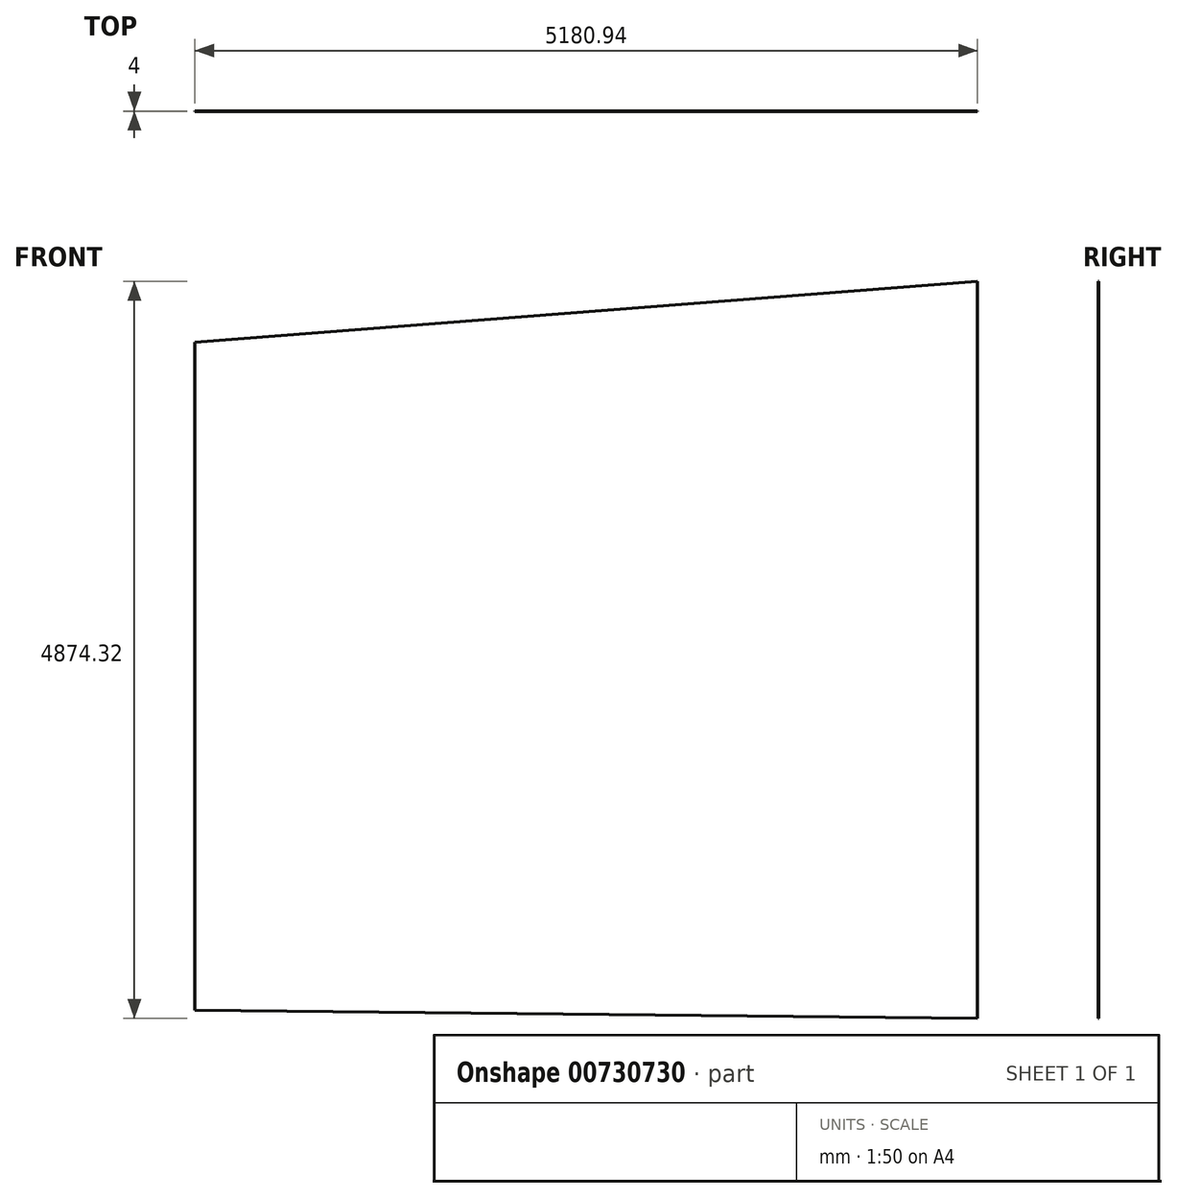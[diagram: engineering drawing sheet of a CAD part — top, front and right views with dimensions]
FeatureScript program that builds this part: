
annotation { "Feature Type Name" : "Feature", "Feature Type Description" : "" }
export const myFeature = defineFeature(function(context is Context, id is Id, definition is map)
    precondition{}
    {
        {
            var Q0;
            Q0=qCreatedBy(makeId("Front.planeOp"),FACE);
            var sketch = newSketch(context, id + "F0", { "sketchPlane" : qUnion([Q0])});
            skLineSegment(sketch, "E0", {"start": v(-2590.47, -2385.26) * mm, "end": v(-2590.47, -175.56) * mm});
            skLineSegment(sketch, "E1", {"start": v(-2590.47, -175.56) * mm, "end": v(-2463.47, -175.56) * mm});
            skLineSegment(sketch, "E2", {"start": v(-2463.47, -175.56) * mm, "end": v(-2590.47, -175.56) * mm});
            skLineSegment(sketch, "E3", {"start": v(-2590.47, -175.56) * mm, "end": v(-2590.47, 2034.16) * mm});
            skLineSegment(sketch, "E4", {"start": v(-2590.47, 2034.16) * mm, "end": v(2590.47, 2437.16) * mm});
            skLineSegment(sketch, "E5", {"start": v(2590.47, 2437.16) * mm, "end": v(2590.47, 0) * mm});
            skLineSegment(sketch, "E6", {"start": v(2590.47, 0) * mm, "end": v(2463.47, 0) * mm});
            skLineSegment(sketch, "E7", {"start": v(2463.47, 0) * mm, "end": v(2590.47, 0) * mm});
            skLineSegment(sketch, "E8", {"start": v(2590.47, 0) * mm, "end": v(2590.47, -2437.16) * mm});
            skLineSegment(sketch, "E9", {"start": v(2590.47, -2437.16) * mm, "end": v(-2590.47, -2385.26) * mm});
            skSolve(sketch);
        }
        {
            var Q0;
            Q0 = qSketchRegion(id + "F0", true);
            extrude(context, id + "F1", {"entities" : qUnion([Q0]), "depth" : 4 * mm, "offsetDistance" : 25 * mm});
        }
    });
